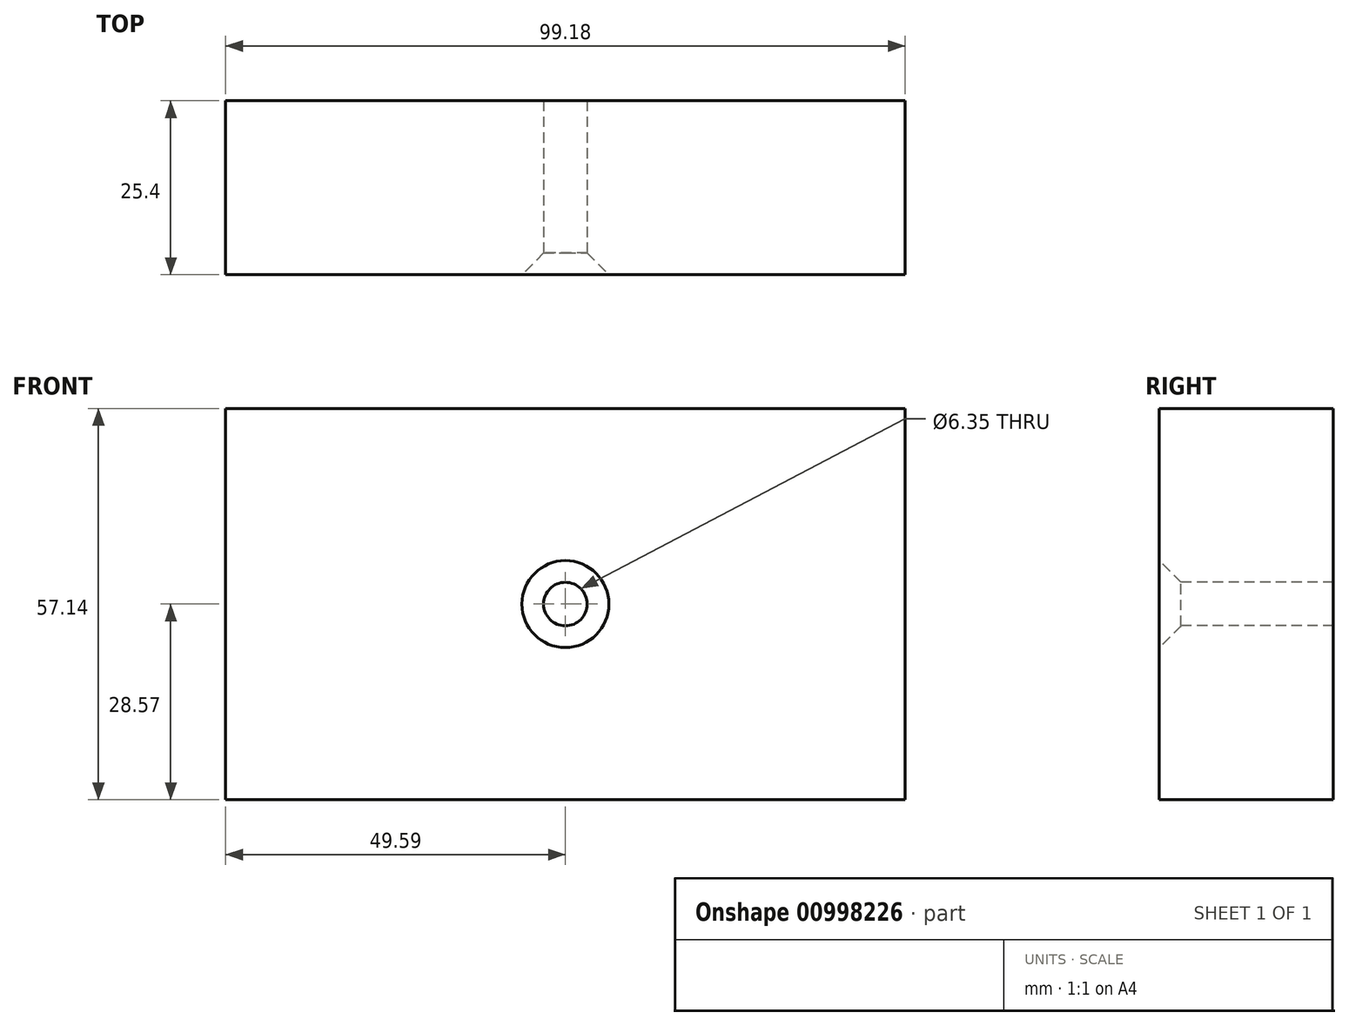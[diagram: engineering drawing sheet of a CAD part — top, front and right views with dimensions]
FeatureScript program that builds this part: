
annotation { "Feature Type Name" : "Feature", "Feature Type Description" : "" }
export const myFeature = defineFeature(function(context is Context, id is Id, definition is map)
    precondition{}
    {
        {
            var Q0;
            Q0=qCreatedBy(makeId("Front.planeOp"),FACE);
            var sketch = newSketch(context, id + "F0", { "sketchPlane" : qUnion([Q0])});
            skLineSegment(sketch, "E0.bottom", {"start": v(49.59, -28.57) * mm, "end": v(-49.59, -28.57) * mm});
            skLineSegment(sketch, "E0.top", {"start": v(49.59, 28.57) * mm, "end": v(-49.59, 28.57) * mm});
            skLineSegment(sketch, "E0.left", {"start": v(49.59, -28.57) * mm, "end": v(49.59, 28.57) * mm});
            skLineSegment(sketch, "E0.right", {"start": v(-49.59, -28.57) * mm, "end": v(-49.59, 28.57) * mm});
            skPoint(sketch, "E0.middle", {"position": v(0, 0) * mm});
            skSolve(sketch);
        }
        {
            var Q0;
            Q0 = qSketchRegion(id + "F0", true);
            extrude(context, id + "F1", {"entities" : qUnion([Q0]), "oppositeDirection" : true, "depth" : 25.4 * mm, "offsetDistance" : 25.4 * mm});
        }
        {
            var Q0;
            Q0=sQuery(id+"F0.wireOp",VERTEX,"E0.middle");
            var Q1;
            Q1=makeQuery(id+"F1.opExtrude","SWEPT_BODY",BODY,{"disambiguationData":[OSD([sQuery(id+"F0.wireOp",EDGE,"E0.bottom"),sQuery(id+"F0.wireOp",EDGE,"E0.top"),sQuery(id+"F0.wireOp",EDGE,"E0.left"),sQuery(id+"F0.wireOp",EDGE,"E0.right")])]});
            hole(context, id + "F2", {"style" : HoleStyle.C_SINK, "endStyle" : HoleEndStyle.THROUGH, "holeDiameter" : 6.35 * mm, "cSinkDiameter" : 12.7 * mm, "cSinkAngle" : 1.57 * radian, "majorDiameter" : 6.35 * mm, "isTappedThrough" : true, "tappedDepth" : 12.7 * mm, "tapClearance" : 3, "locations" : qUnion([Q0]), "scope" : qUnion([Q1])});
        }
    });
